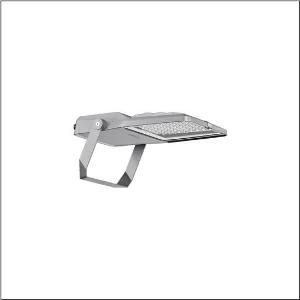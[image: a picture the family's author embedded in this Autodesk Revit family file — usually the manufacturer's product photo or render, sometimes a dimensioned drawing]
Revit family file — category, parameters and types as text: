
# Revit family: floodlight_fl_21_iq_mini___pl61_5xa7771c2c1a_d716
name_source: partatom
category: Lighting Fixtures
units: mm (PartAtom-declared; Revit-internal decimal feet)

## family parameters
Cut with Voids When Loaded = No
Host = Face
Light Source = No
Part Type = Normal
Room Calculation Point = No
Round Connector Dimension = Use Diameter
Shared = No

## types (1)
- --- (1 x LED, 11980 lm, 87.2 W, 3000K)
    Apparent Load = 87 VA
    CIE Flux Codes = 33 65 98 100 100
    Color Rendering = 70
    Color Temperature = 3000K
    Default Elevation = 1800 mm
    Description = Floodlight FL 21 iQ mini, floodlight, primary light control with lens, of PMMA, primary optical cover: protective disc, of toughened safety glass, transparent, light distribution: PL61, light emission: direct distribution, installation type: surface-mounted, LED, High Power LED, rated luminous flux: 11.980lm, luminous efficacy: 137lm/W, light colour: 730, colour temperature: 3000K, control: Auto-Match, Temp-Guard, Lumen-Switch, Night-Set, Smart-Wire, Light-Fading, Desk-Remote (wireless, voltage-free reading and setting of iQ features in the workshop via application-optimized NFC function/RFID function), optimised constant luminous flux control (CLO 2.0), with terminal, 6-pole, mains connection: 220..240V, AC, 50/60Hz, start of lifetime: 87W, end of service life: 92W, reduction: 40W, luminaire housing, of diecast aluminium, powder-coated, Siteco® metallic grey (DB 702S), corrosivity category C5 mid according to DIN EN ISO 12944, sealing non-destructively replaceable, mounting bracket, of steel, galvanised, powder-coated, Siteco® metallic grey (DB 702S), protection rating (complete): IP66, insulation class (complete): insulation class II (safety insulation), certification: CE, ENEC, VDE, protection symbol: D, impact resistance: IK08, permissible operating ambient temperature: -40..+40°C, permissible operating ambient temperature for outdoor applications: -40..+50°C, standard: DIN EN 12944, LABS conformity tested according to VDMA 24364:2018-05, packaging unit: 1 piece

Light Distribution: PL61
    Height = 70 mm
    Lamp = 1 x LED
    Lamp Light Flux = 11980 lm
    Lamp Power = 87.2 W
    Lamp count = 1
    Length = 485 mm
    Luminous efficacy = 137 lm/W
    Manufacturer = Siteco
    ModVariant = No
    Model = 5XA7771C2C1A
    Number of Poles = 1
    OnlyDefault = Yes
    Power Factor = 1
    Product Name = Floodlight FL 21 iQ mini | PL61
    Product group = floodlight | pylon annexe
    ProductGroupID = 6200
    Protection Class = Protection class II
    Protection Degree = IP 66
    RLX_Detail_Level = 1
    RLX_Emergency_Light_Flux = 0 lm
    RLX_Emergency_Type = 0
    RLX_Emergency_Type_DB = No
    RlxData = <blob elided: 96365 chars, md5=e4c7e41d>
    Socket = socket
    Standby Power = 0 W
    System Light Flux = 11980 lm
    System Power = 87 W
    Type Comments = factory setting: luminous flux: 100 % | dim-lin: 254 | 456 mA
    Type Image = l_1006845.jpg
    URL = http://relux.com
    VarID = @adj_124295
    Voltage = 0 V
    Weight = 0.00 kg
    Width = 337 mm

## geometry (parser evidence)
native form markers: Blend x4, Sweep x13
no freeform markers — native parametric forms only
